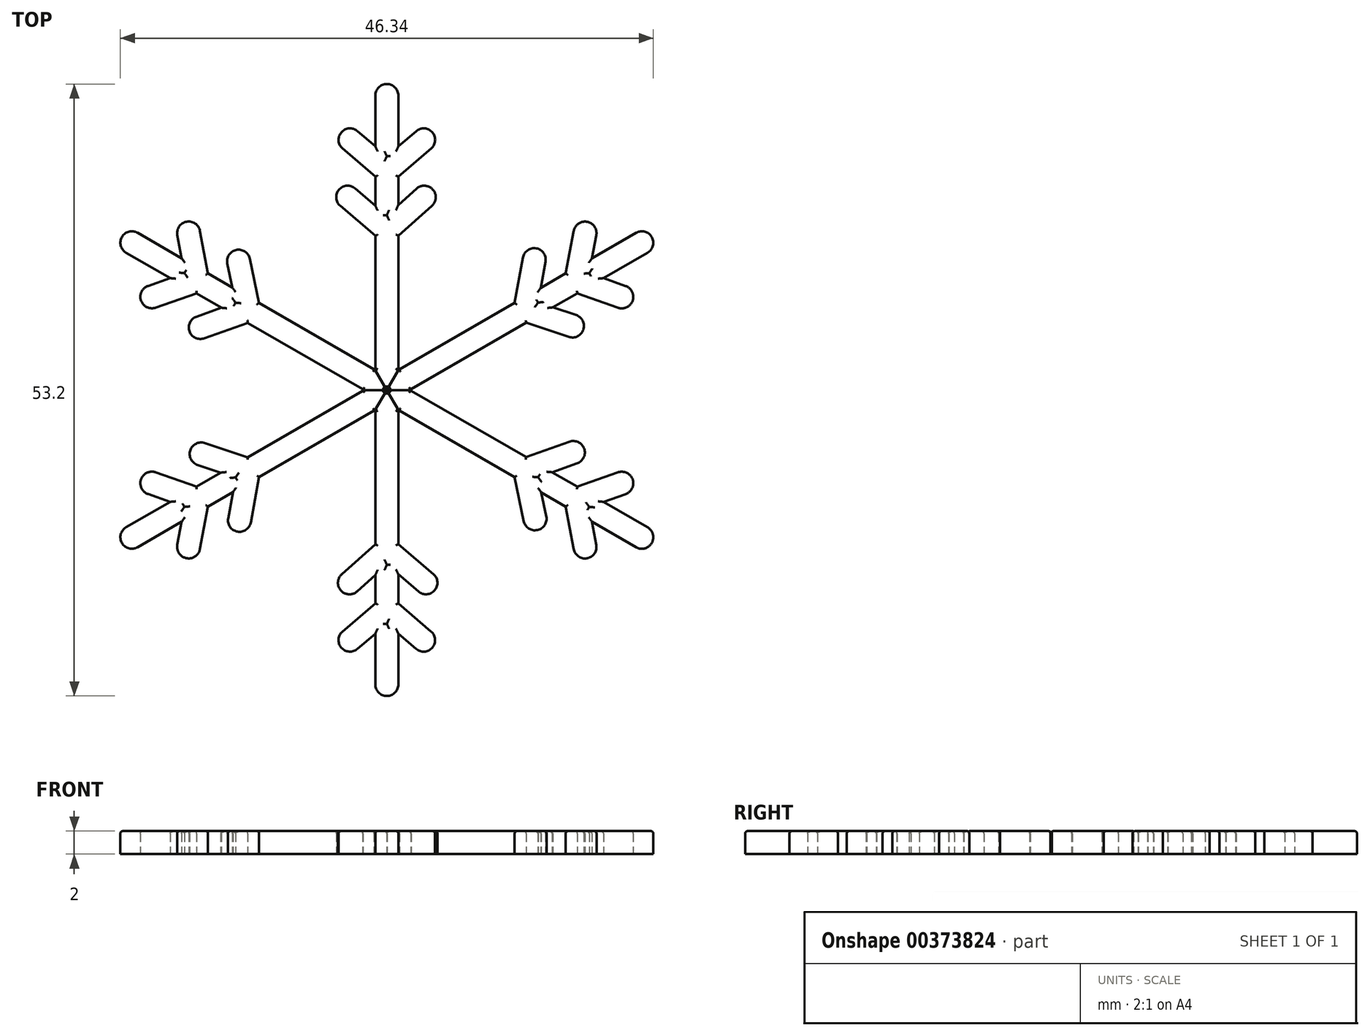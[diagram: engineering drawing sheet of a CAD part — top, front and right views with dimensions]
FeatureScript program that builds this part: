
annotation { "Feature Type Name" : "Feature", "Feature Type Description" : "" }
export const myFeature = defineFeature(function(context is Context, id is Id, definition is map)
    precondition{}
    {
        {
            var Q0;
            Q0=qCreatedBy(makeId("Top.planeOp"),FACE);
            var sketch = newSketch(context, id + "F0", { "sketchPlane" : qUnion([Q0])});
            skLineSegment(sketch, "E0", {"start": v(0, 0) * mm, "end": v(0, 3.42) * mm});
            skLineSegment(sketch, "E1.1.0", {"start": v(0, 0) * mm, "end": v(-1.7, 2.96) * mm});
            skLineSegment(sketch, "E1.2.0", {"start": v(0, 0) * mm, "end": v(-2.96, 1.7) * mm});
            skLineSegment(sketch, "E1.3.0", {"start": v(0, 0) * mm, "end": v(-3.42, 0) * mm});
            skLineSegment(sketch, "E1.4.0", {"start": v(0, 0) * mm, "end": v(-2.96, -1.7) * mm});
            skLineSegment(sketch, "E1.5.0", {"start": v(0, 0) * mm, "end": v(-1.7, -2.96) * mm});
            skPoint(sketch, "E1.center", {"position": v(0, 0) * mm});
            skLineSegment(sketch, "E2.2.6.0", {"start": v(0, 0) * mm, "end": v(0, -3.42) * mm});
            skLineSegment(sketch, "E2.2.7.0", {"start": v(0, 0) * mm, "end": v(1.7, -2.96) * mm});
            skLineSegment(sketch, "E2.2.8.0", {"start": v(0, 0) * mm, "end": v(2.96, -1.7) * mm});
            skLineSegment(sketch, "E2.2.9.0", {"start": v(0, 0) * mm, "end": v(3.42, 0) * mm});
            skLineSegment(sketch, "E2.2.10.0", {"start": v(0, 0) * mm, "end": v(2.96, 1.7) * mm});
            skLineSegment(sketch, "E2.2.11.0", {"start": v(0, 0) * mm, "end": v(1.7, 2.96) * mm});
            skLineSegment(sketch, "E3", {"start": v(0, 3.42) * mm, "end": v(1.04, 1.8) * mm});
            skLineSegment(sketch, "E4", {"start": v(0, 3.42) * mm, "end": v(-1.04, 1.8) * mm});
            skLineSegment(sketch, "E5", {"start": v(0, 3.42) * mm, "end": v(0, 25.6) * mm});
            skLineSegment(sketch, "E6", {"start": v(0, 19) * mm, "end": v(3.2, 21.75) * mm});
            skLineSegment(sketch, "E7", {"start": v(0, 19) * mm, "end": v(-3.2, 21.75) * mm});
            skLineSegment(sketch, "E8.0", {"start": v(1, 1.86) * mm, "end": v(1, 25.6) * mm});
            skLineSegment(sketch, "E9.0", {"start": v(-1, 1.73) * mm, "end": v(-1, 25.6) * mm});
            skCircle(sketch, "E10", {"center": v(0, 25.6) * mm, "radius": 1 * mm});
            skLineSegment(sketch, "E11.0", {"start": v(0.65, 19.76) * mm, "end": v(-2.55, 22.5) * mm});
            skLineSegment(sketch, "E12.0", {"start": v(-0.65, 18.25) * mm, "end": v(-3.85, 20.99) * mm});
            skCircle(sketch, "E13", {"center": v(-3.2, 21.75) * mm, "radius": 1 * mm});
            skLineSegment(sketch, "E14", {"start": v(0, 13.87) * mm, "end": v(-3.4, 16.76) * mm});
            skLineSegment(sketch, "E15", {"start": v(0, 13.87) * mm, "end": v(3.25, 16.76) * mm});
            skLineSegment(sketch, "E16.0", {"start": v(0.65, 14.63) * mm, "end": v(-2.75, 17.53) * mm});
            skLineSegment(sketch, "E17.0", {"start": v(0.67, 13.12) * mm, "end": v(3.92, 16.02) * mm});
            skLineSegment(sketch, "E18.0", {"start": v(-0.67, 14.61) * mm, "end": v(2.59, 17.51) * mm});
            skLineSegment(sketch, "E19.0", {"start": v(-0.65, 13.1) * mm, "end": v(-4.05, 16) * mm});
            skCircle(sketch, "E20", {"center": v(-3.4, 16.76) * mm, "radius": 1 * mm});
            skCircle(sketch, "E21", {"center": v(3.25, 16.76) * mm, "radius": 1 * mm});
            skLineSegment(sketch, "E22.0", {"start": v(0.65, 18.25) * mm, "end": v(3.85, 20.99) * mm});
            skLineSegment(sketch, "E23.0", {"start": v(-0.65, 19.77) * mm, "end": v(2.55, 22.5) * mm});
            skCircle(sketch, "E24", {"center": v(3.2, 21.75) * mm, "radius": 1 * mm});
            skSolve(sketch);
        }
        {
            var Q0;
            Q0 = qSketchRegion(id + "F0", true);
            extrude(context, id + "F1", {"entities" : qUnion([Q0]), "depth" : 2 * mm});
        }
        {
            var Q0;
            Q0=makeQuery(id+"F1.opExtrude","SWEPT_BODY",BODY,{"disambiguationData":[OSD([sQuery(id+"F0.wireOp",EDGE,"E1.1.0"),sQuery(id+"F0.wireOp",EDGE,"E2.2.11.0"),sQuery(id+"F0.wireOp",EDGE,"E3"),sQuery(id+"F0.wireOp",EDGE,"E4"),sQuery(id+"F0.wireOp",EDGE,"E5"),sQuery(id+"F0.wireOp",EDGE,"E8.0"),sQuery(id+"F0.wireOp",EDGE,"E9.0"),sQuery(id+"F0.wireOp",EDGE,"E10"),sQuery(id+"F0.wireOp",EDGE,"E11.0"),sQuery(id+"F0.wireOp",EDGE,"E12.0"),sQuery(id+"F0.wireOp",EDGE,"E13"),sQuery(id+"F0.wireOp",EDGE,"E16.0"),sQuery(id+"F0.wireOp",EDGE,"E17.0"),sQuery(id+"F0.wireOp",EDGE,"E18.0"),sQuery(id+"F0.wireOp",EDGE,"E19.0"),sQuery(id+"F0.wireOp",EDGE,"E20"),sQuery(id+"F0.wireOp",EDGE,"E21"),sQuery(id+"F0.wireOp",EDGE,"E22.0"),sQuery(id+"F0.wireOp",EDGE,"E23.0"),sQuery(id+"F0.wireOp",EDGE,"E24")])]});
            var Q1;
            Q1=makeQuery(id+"F1.opExtrude","SWEPT_EDGE",EDGE,{"disambiguationData":[OSD([sQuery(id+"F0.wireOp",EDGE,"E0"),sQuery(id+"F0.wireOp",EDGE,"E1.1.0"),sQuery(id+"F0.wireOp",EDGE,"E2.2.11.0")])]});
            circularPattern(context, id + "F2", {"entities" : qUnion([Q0]), "axis" : qUnion([Q1]), "angle" : 360 * degree, "instanceCount" : 6, "equalSpace" : true});
        }
        {
            var Q0;
            Q0=makeQuery(id+"F2.opPattern","COPY",FACE,{"derivedFrom":makeQuery(id+"F1.opExtrude","CAP_FACE",FACE,{"disambiguationData":[OSD([sQuery(id+"F0.wireOp",EDGE,"E1.1.0"),sQuery(id+"F0.wireOp",EDGE,"E2.2.11.0"),sQuery(id+"F0.wireOp",EDGE,"E3"),sQuery(id+"F0.wireOp",EDGE,"E4"),sQuery(id+"F0.wireOp",EDGE,"E5"),sQuery(id+"F0.wireOp",EDGE,"E8.0"),sQuery(id+"F0.wireOp",EDGE,"E9.0"),sQuery(id+"F0.wireOp",EDGE,"E10"),sQuery(id+"F0.wireOp",EDGE,"E11.0"),sQuery(id+"F0.wireOp",EDGE,"E12.0"),sQuery(id+"F0.wireOp",EDGE,"E13"),sQuery(id+"F0.wireOp",EDGE,"E16.0"),sQuery(id+"F0.wireOp",EDGE,"E17.0"),sQuery(id+"F0.wireOp",EDGE,"E18.0"),sQuery(id+"F0.wireOp",EDGE,"E19.0"),sQuery(id+"F0.wireOp",EDGE,"E20"),sQuery(id+"F0.wireOp",EDGE,"E21"),sQuery(id+"F0.wireOp",EDGE,"E22.0"),sQuery(id+"F0.wireOp",EDGE,"E23.0"),sQuery(id+"F0.wireOp",EDGE,"E24")])],"isStart":false}),"instanceName":"5"});
            var Q1;
            Q1=makeQuery(id+"F2.opPattern","COPY",FACE,{"derivedFrom":makeQuery(id+"F1.opExtrude","CAP_FACE",FACE,{"disambiguationData":[OSD([sQuery(id+"F0.wireOp",EDGE,"E1.1.0"),sQuery(id+"F0.wireOp",EDGE,"E2.2.11.0"),sQuery(id+"F0.wireOp",EDGE,"E3"),sQuery(id+"F0.wireOp",EDGE,"E4"),sQuery(id+"F0.wireOp",EDGE,"E5"),sQuery(id+"F0.wireOp",EDGE,"E8.0"),sQuery(id+"F0.wireOp",EDGE,"E9.0"),sQuery(id+"F0.wireOp",EDGE,"E10"),sQuery(id+"F0.wireOp",EDGE,"E11.0"),sQuery(id+"F0.wireOp",EDGE,"E12.0"),sQuery(id+"F0.wireOp",EDGE,"E13"),sQuery(id+"F0.wireOp",EDGE,"E16.0"),sQuery(id+"F0.wireOp",EDGE,"E17.0"),sQuery(id+"F0.wireOp",EDGE,"E18.0"),sQuery(id+"F0.wireOp",EDGE,"E19.0"),sQuery(id+"F0.wireOp",EDGE,"E20"),sQuery(id+"F0.wireOp",EDGE,"E21"),sQuery(id+"F0.wireOp",EDGE,"E22.0"),sQuery(id+"F0.wireOp",EDGE,"E23.0"),sQuery(id+"F0.wireOp",EDGE,"E24")])],"isStart":false}),"instanceName":"4"});
            var Q2;
            Q2=makeQuery(id+"F2.opPattern","COPY",FACE,{"derivedFrom":makeQuery(id+"F1.opExtrude","CAP_FACE",FACE,{"disambiguationData":[OSD([sQuery(id+"F0.wireOp",EDGE,"E1.1.0"),sQuery(id+"F0.wireOp",EDGE,"E2.2.11.0"),sQuery(id+"F0.wireOp",EDGE,"E3"),sQuery(id+"F0.wireOp",EDGE,"E4"),sQuery(id+"F0.wireOp",EDGE,"E5"),sQuery(id+"F0.wireOp",EDGE,"E8.0"),sQuery(id+"F0.wireOp",EDGE,"E9.0"),sQuery(id+"F0.wireOp",EDGE,"E10"),sQuery(id+"F0.wireOp",EDGE,"E11.0"),sQuery(id+"F0.wireOp",EDGE,"E12.0"),sQuery(id+"F0.wireOp",EDGE,"E13"),sQuery(id+"F0.wireOp",EDGE,"E16.0"),sQuery(id+"F0.wireOp",EDGE,"E17.0"),sQuery(id+"F0.wireOp",EDGE,"E18.0"),sQuery(id+"F0.wireOp",EDGE,"E19.0"),sQuery(id+"F0.wireOp",EDGE,"E20"),sQuery(id+"F0.wireOp",EDGE,"E21"),sQuery(id+"F0.wireOp",EDGE,"E22.0"),sQuery(id+"F0.wireOp",EDGE,"E23.0"),sQuery(id+"F0.wireOp",EDGE,"E24")])],"isStart":false}),"instanceName":"3"});
            var Q3;
            Q3=makeQuery(id+"F2.opPattern","COPY",FACE,{"derivedFrom":makeQuery(id+"F1.opExtrude","CAP_FACE",FACE,{"disambiguationData":[OSD([sQuery(id+"F0.wireOp",EDGE,"E1.1.0"),sQuery(id+"F0.wireOp",EDGE,"E2.2.11.0"),sQuery(id+"F0.wireOp",EDGE,"E3"),sQuery(id+"F0.wireOp",EDGE,"E4"),sQuery(id+"F0.wireOp",EDGE,"E5"),sQuery(id+"F0.wireOp",EDGE,"E8.0"),sQuery(id+"F0.wireOp",EDGE,"E9.0"),sQuery(id+"F0.wireOp",EDGE,"E10"),sQuery(id+"F0.wireOp",EDGE,"E11.0"),sQuery(id+"F0.wireOp",EDGE,"E12.0"),sQuery(id+"F0.wireOp",EDGE,"E13"),sQuery(id+"F0.wireOp",EDGE,"E16.0"),sQuery(id+"F0.wireOp",EDGE,"E17.0"),sQuery(id+"F0.wireOp",EDGE,"E18.0"),sQuery(id+"F0.wireOp",EDGE,"E19.0"),sQuery(id+"F0.wireOp",EDGE,"E20"),sQuery(id+"F0.wireOp",EDGE,"E21"),sQuery(id+"F0.wireOp",EDGE,"E22.0"),sQuery(id+"F0.wireOp",EDGE,"E23.0"),sQuery(id+"F0.wireOp",EDGE,"E24")])],"isStart":false}),"instanceName":"2"});
            var Q4;
            Q4=makeQuery(id+"F1.opExtrude","CAP_FACE",FACE,{"disambiguationData":[OSD([sQuery(id+"F0.wireOp",EDGE,"E1.1.0"),sQuery(id+"F0.wireOp",EDGE,"E2.2.11.0"),sQuery(id+"F0.wireOp",EDGE,"E3"),sQuery(id+"F0.wireOp",EDGE,"E4"),sQuery(id+"F0.wireOp",EDGE,"E5"),sQuery(id+"F0.wireOp",EDGE,"E8.0"),sQuery(id+"F0.wireOp",EDGE,"E9.0"),sQuery(id+"F0.wireOp",EDGE,"E10"),sQuery(id+"F0.wireOp",EDGE,"E11.0"),sQuery(id+"F0.wireOp",EDGE,"E12.0"),sQuery(id+"F0.wireOp",EDGE,"E13"),sQuery(id+"F0.wireOp",EDGE,"E16.0"),sQuery(id+"F0.wireOp",EDGE,"E17.0"),sQuery(id+"F0.wireOp",EDGE,"E18.0"),sQuery(id+"F0.wireOp",EDGE,"E19.0"),sQuery(id+"F0.wireOp",EDGE,"E20"),sQuery(id+"F0.wireOp",EDGE,"E21"),sQuery(id+"F0.wireOp",EDGE,"E22.0"),sQuery(id+"F0.wireOp",EDGE,"E23.0"),sQuery(id+"F0.wireOp",EDGE,"E24")])],"isStart":false});
            var Q5;
            Q5=makeQuery(id+"F2.opPattern","COPY",FACE,{"derivedFrom":makeQuery(id+"F1.opExtrude","CAP_FACE",FACE,{"disambiguationData":[OSD([sQuery(id+"F0.wireOp",EDGE,"E1.1.0"),sQuery(id+"F0.wireOp",EDGE,"E2.2.11.0"),sQuery(id+"F0.wireOp",EDGE,"E3"),sQuery(id+"F0.wireOp",EDGE,"E4"),sQuery(id+"F0.wireOp",EDGE,"E5"),sQuery(id+"F0.wireOp",EDGE,"E8.0"),sQuery(id+"F0.wireOp",EDGE,"E9.0"),sQuery(id+"F0.wireOp",EDGE,"E10"),sQuery(id+"F0.wireOp",EDGE,"E11.0"),sQuery(id+"F0.wireOp",EDGE,"E12.0"),sQuery(id+"F0.wireOp",EDGE,"E13"),sQuery(id+"F0.wireOp",EDGE,"E16.0"),sQuery(id+"F0.wireOp",EDGE,"E17.0"),sQuery(id+"F0.wireOp",EDGE,"E18.0"),sQuery(id+"F0.wireOp",EDGE,"E19.0"),sQuery(id+"F0.wireOp",EDGE,"E20"),sQuery(id+"F0.wireOp",EDGE,"E21"),sQuery(id+"F0.wireOp",EDGE,"E22.0"),sQuery(id+"F0.wireOp",EDGE,"E23.0"),sQuery(id+"F0.wireOp",EDGE,"E24")])],"isStart":false}),"instanceName":"1"});
            fillet(context, id + "F3", {"entities" : qUnion([Q0, Q1, Q2, Q3, Q4, Q5]), "radius" : 0.2 * mm, "tangentPropagation" : true, "allowEdgeOverflow" : false});
        }
    });
